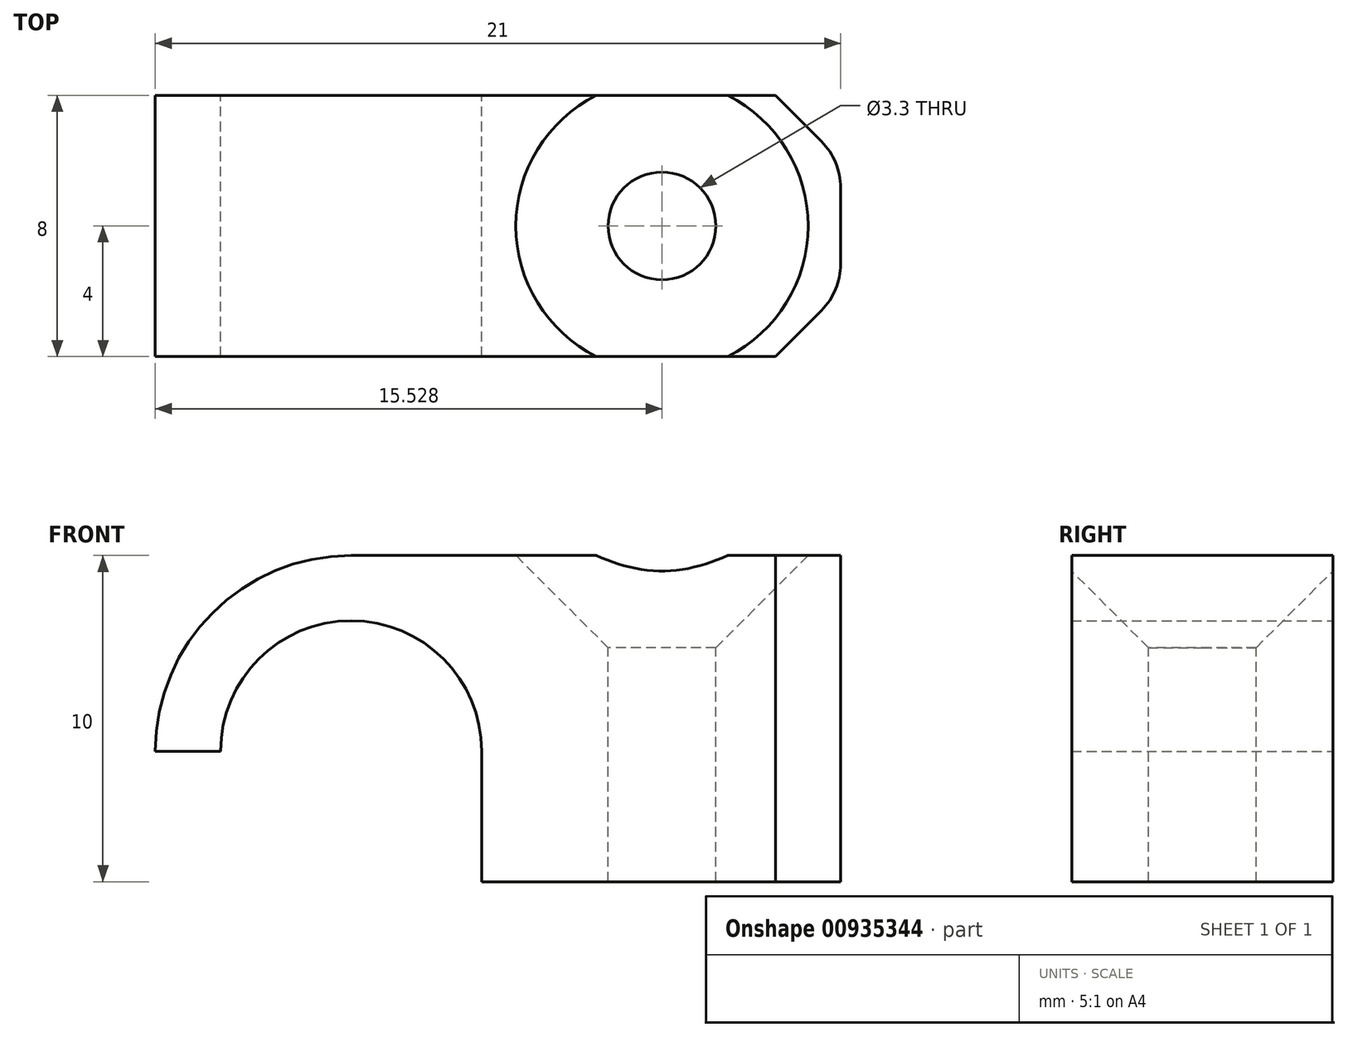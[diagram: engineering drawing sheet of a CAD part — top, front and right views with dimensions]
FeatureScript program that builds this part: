
annotation { "Feature Type Name" : "Feature", "Feature Type Description" : "" }
export const myFeature = defineFeature(function(context is Context, id is Id, definition is map)
    precondition{}
    {
        {
            var Q0;
            Q0=qCreatedBy(makeId("Front.planeOp"),FACE);
            var sketch = newSketch(context, id + "F0", { "sketchPlane" : qUnion([Q0])});
            skArc(sketch, "E0", {"start": v(4, 0) * mm, "mid": v(0, 4) * mm, "end": v(-4, 0) * mm});
            skArc(sketch, "E1.0", {"start": v(0, 6) * mm, "mid": v(-4.24, 4.24) * mm, "end": v(-6, 0) * mm});
            skLineSegment(sketch, "E2", {"start": v(-6, 0) * mm, "end": v(-4, 0) * mm});
            skLineSegment(sketch, "E3", {"start": v(0, 6) * mm, "end": v(15, 6) * mm});
            skPoint(sketch, "E4.start.orphan", {"position": v(4, 0) * mm});
            skLineSegment(sketch, "E5", {"start": v(4, 0) * mm, "end": v(4, -4) * mm});
            skLineSegment(sketch, "E6", {"start": v(4, -4) * mm, "end": v(15, -4) * mm});
            skLineSegment(sketch, "E7", {"start": v(15, -4) * mm, "end": v(15, 6) * mm});
            skPoint(sketch, "E8.orphan", {"position": v(0, -4) * mm});
            skSolve(sketch);
        }
        {
            var Q0;
            Q0=makeQuery(id+"F0.imprint","IMPRINT",FACE,{"disambiguationData":[TD([[makeQuery(id+"F0.imprint","IMPRINT",EDGE,{"derivedFrom":sQuery(id+"F0.wireOp",EDGE,"E0")}),-1.0]])]});
            extrude(context, id + "F1", {"entities" : qUnion([Q0]), "endBound" : BoundingType.SYMMETRIC, "depth" : 8 * mm, "offsetDistance" : 25 * mm});
        }
        {
            var Q0;
            Q0=makeQuery(id+"F1.opExtrude","SWEPT_FACE",FACE,{"disambiguationData":[OSD([sQuery(id+"F0.wireOp",EDGE,"E3")])]});
            var sketch = newSketch(context, id + "F2", { "sketchPlane" : qUnion([Q0])});
            skLineSegment(sketch, "E9", {"start": v(15, -4) * mm, "end": v(4.06, 4) * mm, "construction": true});
            skPoint(sketch, "E10", {"position": v(9.53, 0) * mm});
            skSolve(sketch);
        }
        {
            var Q0;
            Q0=sQuery(id+"F2.wireOp",VERTEX,"E10");
            var Q1;
            Q1=makeQuery(id+"F1.opExtrude","SWEPT_BODY",BODY,{"disambiguationData":[OSD([sQuery(id+"F0.wireOp",EDGE,"E0"),sQuery(id+"F0.wireOp",EDGE,"E1.0"),sQuery(id+"F0.wireOp",EDGE,"E2"),sQuery(id+"F0.wireOp",EDGE,"E3"),sQuery(id+"F0.wireOp",EDGE,"E5"),sQuery(id+"F0.wireOp",EDGE,"E6"),sQuery(id+"F0.wireOp",EDGE,"E7")])]});
            hole(context, id + "F3", {"style" : HoleStyle.C_SINK, "endStyle" : HoleEndStyle.THROUGH, "standardTappedOrClearance" : lookupTablePath({ "standard" : "ISO", "engagement" : "75%", "pitch" : "0.7 mm", "size" : "M4", "type" : "Tapped" }), "standardBlindInLast" : lookupTablePath({ "standard" : "ISO", "fit" : "Normal", "engagement" : "75%", "pitch" : "0.7 mm", "size" : "M4", "type" : "Clearance & tapped" }), "holeDiameter" : 3.3 * mm, "cSinkDiameter" : 8.96 * mm, "cSinkAngle" : 90 * degree, "majorDiameter" : 4 * mm, "showTappedDepth" : true, "isTappedThrough" : true, "tappedDepth" : 12 * mm, "tapClearance" : 3, "locations" : qUnion([Q0]), "scope" : qUnion([Q1])});
        }
        {
            var Q0;
            Q0=makeQuery(id+"F1.opExtrude","CAP_EDGE",EDGE,{"disambiguationData":[OSD([sQuery(id+"F0.wireOp",EDGE,"E7")])],"isStart":true});
            var Q1;
            Q1=makeQuery(id+"F1.opExtrude","CAP_EDGE",EDGE,{"disambiguationData":[OSD([sQuery(id+"F0.wireOp",EDGE,"E7")])],"isStart":false});
            chamfer(context, id + "F4", {"entities" : qUnion([Q0, Q1]), "width" : 2 * mm, "tangentPropagation" : true});
        }
        {
            var Q0;
            {var subQ0=sQuery(id+"F0.wireOp",EDGE,"E7");Q0=makeQuery(id+"F4.opChamfer","BLEND_EDGE",EDGE,{"blendedFrom":[makeQuery(id+"F1.opExtrude","CAP_EDGE",EDGE,{"disambiguationData":[OSD([subQ0])],"isStart":false}),makeQuery(id+"F1.opExtrude","SWEPT_FACE",FACE,{"disambiguationData":[OSD([subQ0])]})],"blendedInto":[makeQuery(id+"F1.opExtrude","SWEPT_FACE",FACE,{"disambiguationData":[OSD([subQ0])]})]});}
            var Q1;
            {var subQ0=sQuery(id+"F0.wireOp",EDGE,"E7");Q1=makeQuery(id+"F4.opChamfer","BLEND_EDGE",EDGE,{"blendedFrom":[makeQuery(id+"F1.opExtrude","CAP_EDGE",EDGE,{"disambiguationData":[OSD([subQ0])],"isStart":true}),makeQuery(id+"F1.opExtrude","SWEPT_FACE",FACE,{"disambiguationData":[OSD([subQ0])]})],"blendedInto":[makeQuery(id+"F1.opExtrude","SWEPT_FACE",FACE,{"disambiguationData":[OSD([subQ0])]})]});}
            fillet(context, id + "F5", {"entities" : qUnion([Q0, Q1]), "radius" : 2 * mm, "tangentPropagation" : true, "allowEdgeOverflow" : false});
        }
    });
